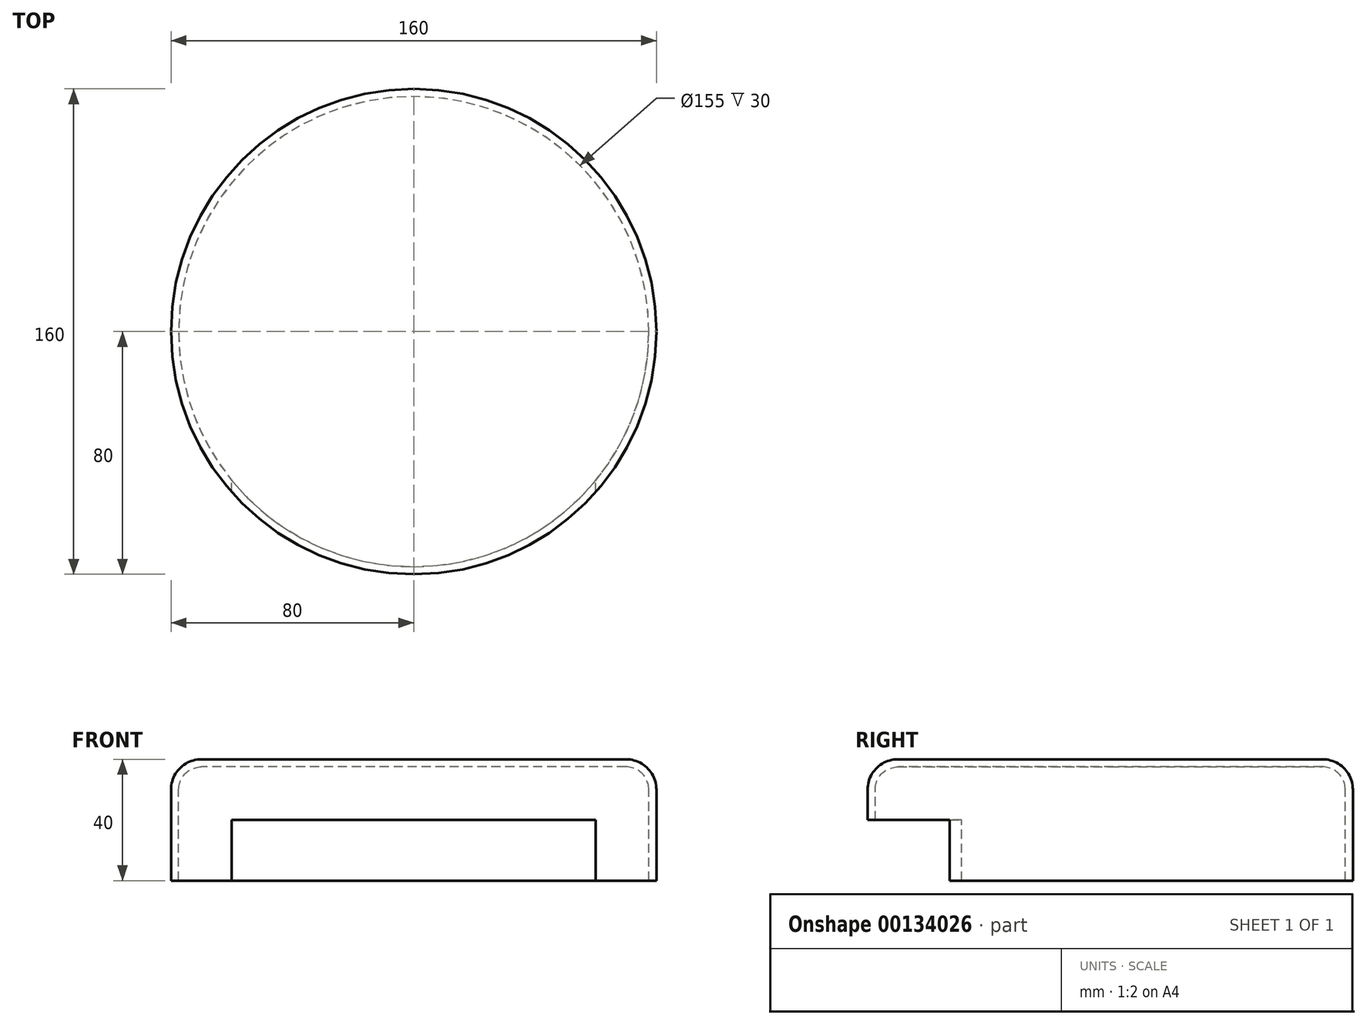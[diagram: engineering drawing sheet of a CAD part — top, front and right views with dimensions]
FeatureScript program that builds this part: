
annotation { "Feature Type Name" : "Feature", "Feature Type Description" : "" }
export const myFeature = defineFeature(function(context is Context, id is Id, definition is map)
    precondition{}
    {
        {
            var Q0;
            Q0=qCreatedBy(makeId("Right.planeOp"),FACE);
            var sketch = newSketch(context, id + "F0", { "sketchPlane" : qUnion([Q0])});
            skLineSegment(sketch, "E0", {"start": v(-80, -40) * mm, "end": v(-80, -10) * mm});
            skLineSegment(sketch, "E1", {"start": v(-70, 0) * mm, "end": v(0, 0) * mm});
            skPoint(sketch, "E2.visualSharp", {"position": v(-80, 0) * mm});
            skArc(sketch, "E2.filletArc", {"start": v(-70, 0) * mm, "mid": v(-77.07, -2.93) * mm, "end": v(-80, -10) * mm});
            skLineSegment(sketch, "E3", {"start": v(-80, -40) * mm, "end": v(0, -40) * mm});
            skLineSegment(sketch, "E4", {"start": v(0, 0) * mm, "end": v(0, -40) * mm});
            skSolve(sketch);
        }
        {
            var Q0;
            Q0=makeQuery(id+"F0.imprint","IMPRINT",FACE,{"disambiguationData":[TD([[makeQuery(id+"F0.imprint","IMPRINT",EDGE,{"derivedFrom":sQuery(id+"F0.wireOp",EDGE,"E0")}),-1.0]])]});
            var Q1;
            Q1=sQuery(id+"F0.wireOp",EDGE,"E4");
            revolve(context, id + "F1", {"entities" : qUnion([Q0]), "axis" : qUnion([Q1]), "revolveType" : RevolveType.FULL});
        }
        {
            var Q0;
            Q0=makeQuery(id+"F1.opRevolve","SWEPT_FACE",FACE,{"disambiguationData":[OSD([sQuery(id+"F0.wireOp",EDGE,"E3")])]});
            shell(context, id + "F2", {"entities" : qUnion([Q0]), "thickness" : 2.5 * mm});
        }
        {
            var Q0;
            Q0=qCreatedBy(makeId("Front.planeOp"),FACE);
            var sketch = newSketch(context, id + "F3", { "sketchPlane" : qUnion([Q0])});
            skLineSegment(sketch, "E5.bottom", {"start": v(-60, -50) * mm, "end": v(60, -50) * mm});
            skLineSegment(sketch, "E5.top", {"start": v(-60, -20) * mm, "end": v(60, -20) * mm});
            skLineSegment(sketch, "E5.left", {"start": v(-60, -50) * mm, "end": v(-60, -20) * mm});
            skLineSegment(sketch, "E5.right", {"start": v(60, -50) * mm, "end": v(60, -20) * mm});
            skSolve(sketch);
        }
        {
            var Q0;
            Q0=makeQuery(id+"F3.imprint","IMPRINT",FACE,{"disambiguationData":[TD([[makeQuery(id+"F3.imprint","IMPRINT",EDGE,{"derivedFrom":sQuery(id+"F3.wireOp",EDGE,"E5.bottom")}),1.0]])]});
            extrude(context, id + "F4", {"entities" : qUnion([Q0]), "operationType" : NewBodyOperationType.REMOVE, "depth" : 100 * mm});
        }
    });
